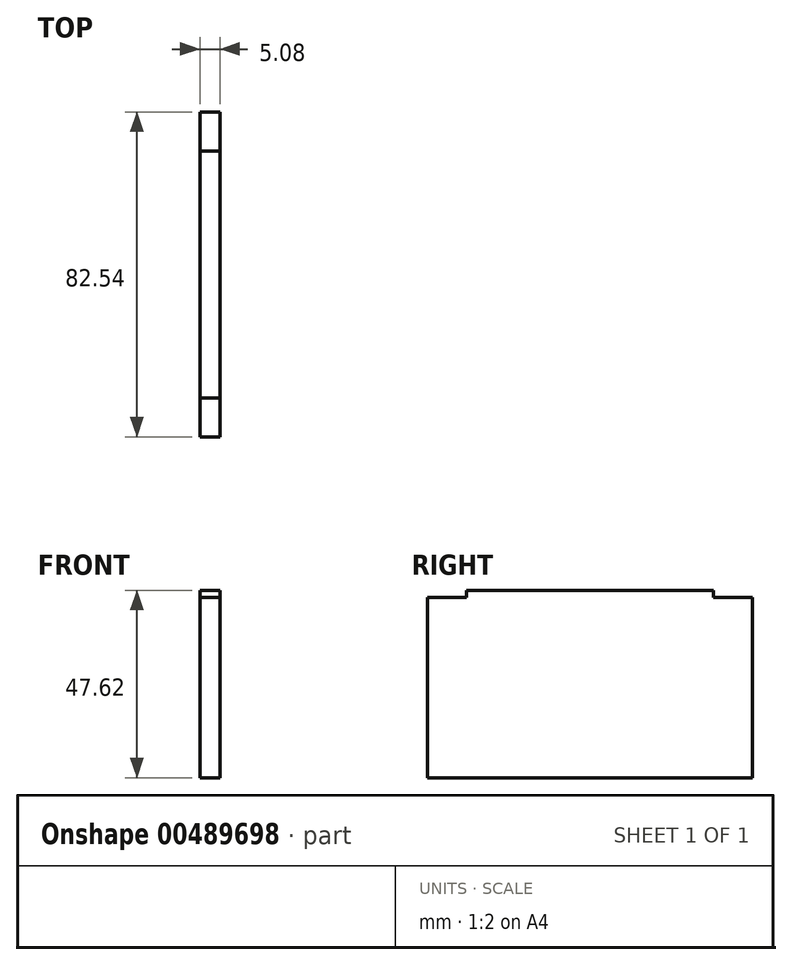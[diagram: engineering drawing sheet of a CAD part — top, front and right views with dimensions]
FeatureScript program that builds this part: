
annotation { "Feature Type Name" : "Feature", "Feature Type Description" : "" }
export const myFeature = defineFeature(function(context is Context, id is Id, definition is map)
    precondition{}
    {
        {
            var Q0;
            Q0=qCreatedBy(makeId("Right.planeOp"),FACE);
            var sketch = newSketch(context, id + "F0", { "sketchPlane" : qUnion([Q0])});
            skLineSegment(sketch, "E0.bottom", {"start": v(41.28, -23.81) * mm, "end": v(-41.28, -23.81) * mm});
            skLineSegment(sketch, "E0.top", {"start": v(31.37, 23.81) * mm, "end": v(-31.37, 23.81) * mm});
            skLineSegment(sketch, "E0.left", {"start": v(41.28, -23.81) * mm, "end": v(41.28, 22.03) * mm});
            skLineSegment(sketch, "E0.right", {"start": v(-41.28, -23.81) * mm, "end": v(-41.28, 22.03) * mm});
            skPoint(sketch, "E0.middle", {"position": v(0, 0) * mm});
            skLineSegment(sketch, "E1", {"start": v(-41.28, 22.03) * mm, "end": v(-31.37, 22.03) * mm});
            skLineSegment(sketch, "E2", {"start": v(-31.37, 22.03) * mm, "end": v(-31.37, 23.81) * mm});
            skLineSegment(sketch, "E3", {"start": v(41.28, 22.03) * mm, "end": v(31.37, 22.03) * mm});
            skPoint(sketch, "E4.end.orphan", {"position": v(31.37, 23.81) * mm});
            skPoint(sketch, "E5.orphan", {"position": v(41.28, 23.81) * mm});
            skPoint(sketch, "E6.orphan", {"position": v(-41.28, 23.81) * mm});
            skLineSegment(sketch, "E7", {"start": v(31.37, 23.81) * mm, "end": v(31.37, 22.03) * mm});
            skSolve(sketch);
        }
        {
            var Q0;
            Q0=makeQuery(id+"F0.imprint","IMPRINT",FACE,{"disambiguationData":[TD([[makeQuery(id+"F0.imprint","IMPRINT",EDGE,{"derivedFrom":sQuery(id+"F0.wireOp",EDGE,"E0.bottom")}),-1.0]])]});
            extrude(context, id + "F1", {"entities" : qUnion([Q0]), "depth" : 5.08 * mm});
        }
    });
